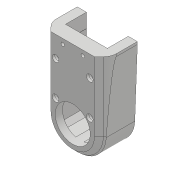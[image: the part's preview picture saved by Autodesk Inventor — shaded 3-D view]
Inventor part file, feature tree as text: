
AUTODESK INVENTOR PART (.ipt)
format: ipt  version: 2018 (Build 220112000, 112)  size: 725,504 bytes
history: native  units: mm
features: sketch x34, projected_geometry x31, extrude x27, hole x9, fillet x7, chamfer x3, mirror x1
ambient origin geometry x8: Origin, YZ Plane, XZ Plane, XY Plane, X Axis, Y Axis, Z Axis, Center Point
bodies: Solid1 (feature_tree)
feature tree (112):
  extrude  "Extrusion1"  Depth=45.0mm
  extrude  "Extrusion2"  Depth=2.25mm
  hole  "Hole1"  [1 undecoded]
  hole  "Hole2"  [1 undecoded]
  fillet  "Fillet1"  Radius=14.0mm
  extrude  "Extrusion3"  Depth=18.5mm
  extrude  "Extrusion4"  Depth=10.0mm
  extrude  "Extrusion5"  Depth=2.0mm
  extrude  "Extrusion6"  Depth=2.0mm
  hole  "Hole3"  [1 undecoded]
  extrude  "Extrusion7"  Depth=0.5mm
  extrude  "Extrusion8"  Depth=5.0mm TaperAngle=0.0deg
  extrude  "Extrusion9"  Depth=10.0mm
  extrude  "Extrusion10"  Depth=10.0mm
  extrude  "Extrusion11"  Depth=14.5mm
  extrude  "Extrusion12"  Depth=14.5mm
  extrude  "Extrusion13"  Depth=5.0mm
  extrude  "Extrusion14"  Depth=5.0mm
  extrude  "Extrusion15"  Depth=5.0mm
  extrude  "Extrusion16"  Depth=5.0mm
  extrude  "Extrusion17"  Depth=1.0mm
  chamfer  "Chamfer1"  Distance=1.0mm
  fillet  "Fillet7"  Radius=20.7mm
  fillet  "Fillet8"  Radius=32.0mm
  mirror  "Mirror1"
  extrude  "Extrusion19"  Depth=1.0mm TaperAngle=0.0deg
  extrude  "Extrusion20"  Depth=8.0mm
  extrude  "Extrusion21"  Depth=0.2mm TaperAngle=0.0deg
  extrude  "Extrusion22"  Depth=0.5mm TaperAngle=0.0deg
  extrude  "Extrusion23"  Depth=5.0mm TaperAngle=0.0deg
  chamfer  "Chamfer2"  Distance=5.0mm
  fillet  "Fillet9"  Radius=0.2mm
  extrude  "Extrusion24"  Depth=2.0mm TaperAngle=45.0deg
  extrude  "Extrusion27"  Depth=0.5mm
  extrude  "Extrusion28"  Depth=1.8mm TaperAngle=0.0deg
  hole  "Hole6"  [1 undecoded]
  sketch  "Sketch39"  dims[d105=1.5mm d114=0.5mm]
  hole  "Hole7"  [1 undecoded]
  hole  "Hole8"  [1 undecoded]
  fillet  "Fillet10"  Radius=5.0mm
  hole  "Hole9"  [1 undecoded]
  extrude  "Extrusion29"  Depth=20.75mm
  chamfer  "Chamfer4"  Distance=10.0mm
  hole  "Hole10"  [1 undecoded]
  fillet  "Fillet11"  Radius=18.0mm
  hole  "Hole11"  [1 undecoded]
  fillet  "Fillet12"  Radius=0.05mm
  extrude  "Extrusion30"  Depth=7.0mm TaperAngle=0.0deg
  sketch  "Sketch1"  dims[d0=24.5mm d1=45.0mm]
  sketch  "Sketch2"  dims[d2=1.95mm d3=0.0mm d4=2.25mm]
  projected_geometry  "Projected Loop1"
  sketch  "Sketch3"  dims[d5=20.0mm d6=2.25mm]
  projected_geometry  "Projected Loop2"
  sketch  "Sketch4"  dims[d7=5.25mm d8=5.25mm d9=14.0mm]
  projected_geometry  "Projected Loop3"
  sketch  "Sketch5"  dims[d10=5.25mm d11=18.5mm]
  projected_geometry  "Projected Loop4"
  sketch  "Sketch6"  dims[d12=10.0mm d13=0.0mm d14=20.5mm]
  projected_geometry  "Projected Loop5"
  sketch  "Sketch7"  dims[d15=2.0mm d16=2.195mm]
  projected_geometry  "Projected Loop6"
  sketch  "Sketch8"  dims[d17=2.0mm]
  projected_geometry  "Projected Loop7"
  sketch  "Sketch9"  dims[d18=2.4mm d19=6.0mm d20=4.4mm d21=2.0mm d22=90.0deg d23=8.0mm d24=20.594885mm d25=20.5mm]
  projected_geometry  "Projected Loop8"
  projected_geometry  "Projected Loop9"
  sketch  "Sketch10"  dims[d26=26.65mm d27=2.0mm]
  projected_geometry  "Projected Loop10"
  projected_geometry  "Projected Loop11"
  sketch  "Sketch11"  dims[d28=2.0mm]
  projected_geometry  "Projected Loop12"
  sketch  "Sketch12"  dims[d29=2.4mm d30=6.0mm d31=4.4mm d32=2.0mm d33=90.0deg d34=8.0mm d35=20.594885mm d36=0.5mm]
  sketch  "Sketch13"  dims[d37=18.0mm d38=5.0mm d39=0.0mm]
  sketch  "Sketch14"  dims[d41=10.0mm d42=0.0mm d43=24.5mm]
  projected_geometry  "Projected Loop13"
  sketch  "Sketch15"  dims[d44=1.15mm d45=0.0mm d46=10.0mm]
  sketch  "Sketch16"  dims[d47=21.0mm d48=14.5mm]
  projected_geometry  "Projected Loop14"
  sketch  "Sketch17"  dims[d49=20.0mm d50=14.5mm]
  projected_geometry  "Projected Loop15"
  sketch  "Sketch18"  dims[d51=24.5mm d52=5.0mm]
  projected_geometry  "Projected Loop16"
  sketch  "Sketch19"  dims[d53=5.0mm d54=2.25mm]
  projected_geometry  "Projected Loop17"
  sketch  "Sketch20"  dims[d55=2.25mm d56=5.0mm]
  projected_geometry  "Projected Loop18"
  sketch  "Sketch25"  dims[d57=5.0mm d58=9.0mm]
  projected_geometry  "Projected Loop22"
  sketch  "Sketch26"  dims[d59=14.75mm d60=4.0mm d61=1.0mm d62=0.0mm d63=20.7mm]
  projected_geometry  "Projected Loop23"
  sketch  "Sketch27"  dims[d64=2.4mm d65=6.0mm d66=4.4mm d67=2.0mm d68=90.0deg d69=8.0mm d70=20.594885mm d72=32.0mm]
  projected_geometry  "Projected Loop25"
  sketch  "Sketch29"  dims[d73=5.0mm d74=0.0mm d75=1.0mm d76=0.0mm]
  projected_geometry  "Projected Loop26"
  sketch  "Sketch30"  dims[d77=12.25mm d78=0.0mm d80=8.0mm]
  projected_geometry  "Projected Loop27"
  sketch  "Sketch32"  dims[d81=4.5mm d82=0.0mm d84=0.2mm d85=0.0mm]
  projected_geometry  "Projected Loop28"
  projected_geometry  "Projected Loop29"
  sketch  "Sketch36"  dims[d86=21.0mm d87=0.5mm d88=0.0mm]
  projected_geometry  "Projected Loop33"
  sketch  "Sketch37"  dims[d91=8.0mm d92=0.0mm d93=5.0mm d94=0.0mm d95=5.0mm d96=0.0mm d98=0.2mm d99=0.0mm]
  projected_geometry  "Projected Loop34"
  sketch  "Sketch38"  dims[d100=0.2mm d101=0.0mm d102=2.5mm d103=2.0mm d104=45.0deg]
  projected_geometry  "Projected Loop35"
  sketch  "Sketch41"  dims[d128=1.8mm d129=0.0mm d130=1.8mm d131=0.0mm]
  projected_geometry  "Projected Loop36"
  sketch  "Sketch42"  dims[d133=36.055mm d134=4.2225mm]
  projected_geometry  "Projected Loop37"
  sketch  "Sketch43"  dims[d135=4.2225mm d136=2.0mm d137=0.0mm]
  projected_geometry  "Projected Loop38"
  sketch  "Sketch44"  dims[d138=2.0mm d139=0.0mm d140=2.0mm d141=0.0mm d142=5.0mm d143=2.0mm d144=45.0deg d145=8.0mm d147=33.0mm d148=10.0mm d149=0.0mm d161=20.75mm d162=18.0mm d163=25.0mm d164=0.05mm d165=7.0mm d166=0.0mm d167=1.5mm d168=0.0mm d169=3.0mm d170=12.0mm d171=2.1mm d172=6.0mm d173=6.3mm d174=2.0mm d175=90.0deg d176=8.0mm d177=20.594885mm d178=1.567mm d179=36.0mm d180=4.4mm d181=2.0mm d182=90.0deg d183=36.0mm d184=20.594885mm d185=4.0mm d186=5.029mm d187=4.4mm d188=2.0mm d189=90.0deg d190=15.0mm d191=0.0mm d192=0.5mm d193=2.1mm d194=5.029mm d195=4.4mm d196=2.0mm d197=90.0deg d198=20.75mm d199=0.0mm d200=15.0mm d201=1.5mm d202=0.0mm d203=1.5mm d204=2.0mm d205=45.0deg d206=4.0mm d207=5.029mm d208=4.4mm d209=2.0mm d210=90.0deg d211=2.2mm d212=0.0mm d213=0.75mm d214=4.0mm d215=5.029mm d216=4.4mm d217=2.0mm d218=90.0deg d219=2.2mm d220=0.0mm d221=0.75mm d222=20.75mm d223=0.0mm]
note: 9 required parameter values undecoded (feature->parameter linkage not recoverable at this tier; creation-order binding heuristic only, values carry confidence <= 0.55)
